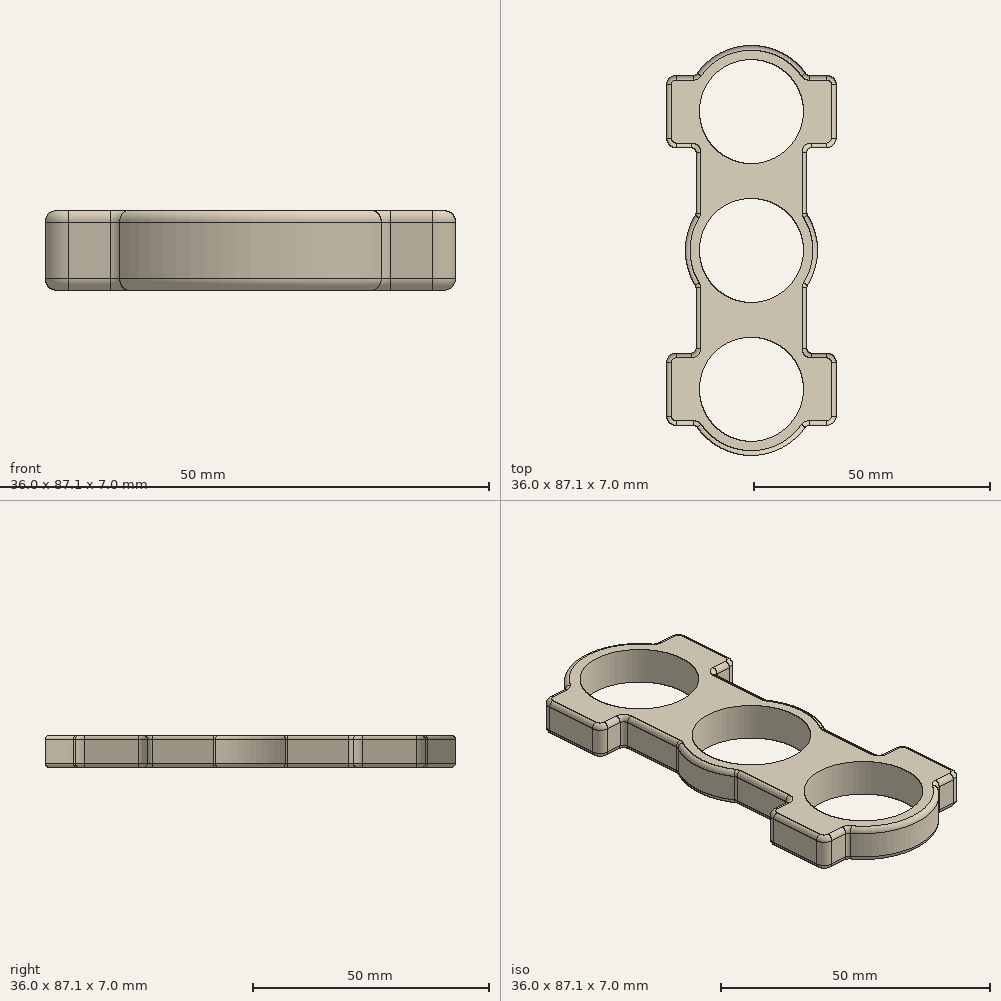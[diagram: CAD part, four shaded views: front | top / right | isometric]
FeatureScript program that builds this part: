
annotation { "Feature Type Name" : "Feature", "Feature Type Description" : "" }
export const myFeature = defineFeature(function(context is Context, id is Id, definition is map)
    precondition{}
    {
        {
            var Q0;
            Q0=qCreatedBy(makeId("Top.planeOp"),FACE);
            var sketch = newSketch(context, id + "F0", { "sketchPlane" : qUnion([Q0])});
            skCircle(sketch, "E0", {"center": v(0, 0) * mm, "radius": 11.05 * mm});
            skArc(sketch, "E1.0", {"start": v(-11.93, 7.43) * mm, "mid": v(0, -14.05) * mm, "end": v(11.93, 7.43) * mm});
            skLineSegment(sketch, "E2", {"start": v(0, 0) * mm, "end": v(0, 29.5) * mm, "construction": true});
            skCircle(sketch, "E3", {"center": v(0, 29.5) * mm, "radius": 11.05 * mm});
            skArc(sketch, "E4.0", {"start": v(11.49, 37.59) * mm, "mid": v(0, 43.55) * mm, "end": v(-11.49, 37.59) * mm});
            skLineSegment(sketch, "E5.bottom", {"start": v(18, 37.17) * mm, "end": v(12.3, 37.17) * mm});
            skLineSegment(sketch, "E5.top", {"start": v(18, 21.83) * mm, "end": v(12.77, 21.83) * mm});
            skLineSegment(sketch, "E5.left", {"start": v(18, 37.17) * mm, "end": v(18, 21.83) * mm});
            skLineSegment(sketch, "E5.right", {"start": v(-18, 37.17) * mm, "end": v(-18, 21.83) * mm});
            skLineSegment(sketch, "E6", {"start": v(-11.77, 20.83) * mm, "end": v(-11.77, 7.96) * mm});
            skLineSegment(sketch, "E7", {"start": v(11.77, 20.83) * mm, "end": v(11.77, 7.96) * mm});
            skLineSegment(sketch, "E8.trimOffspring", {"start": v(-12.77, 21.83) * mm, "end": v(-18, 21.83) * mm});
            skLineSegment(sketch, "E9.trimOffspring", {"start": v(-12.3, 37.17) * mm, "end": v(-18, 37.17) * mm});
            skPoint(sketch, "E10.visualSharp", {"position": v(-11.77, 21.83) * mm});
            skArc(sketch, "E10.filletArc", {"start": v(-11.77, 20.83) * mm, "mid": v(-12.07, 21.54) * mm, "end": v(-12.77, 21.83) * mm});
            skPoint(sketch, "E11.visualSharp", {"position": v(11.77, 21.83) * mm});
            skArc(sketch, "E11.filletArc", {"start": v(12.77, 21.83) * mm, "mid": v(12.07, 21.54) * mm, "end": v(11.77, 20.83) * mm});
            skPoint(sketch, "E12.visualSharp", {"position": v(-11.77, 37.17) * mm});
            skArc(sketch, "E12.filletArc", {"start": v(-12.3, 37.17) * mm, "mid": v(-11.84, 37.28) * mm, "end": v(-11.49, 37.59) * mm});
            skPoint(sketch, "E13.visualSharp", {"position": v(11.77, 37.17) * mm});
            skArc(sketch, "E13.filletArc", {"start": v(11.49, 37.59) * mm, "mid": v(11.84, 37.28) * mm, "end": v(12.3, 37.17) * mm});
            skPoint(sketch, "E14.visualSharp", {"position": v(-11.77, 7.67) * mm});
            skArc(sketch, "E14.filletArc", {"start": v(-11.93, 7.43) * mm, "mid": v(-11.81, 7.68) * mm, "end": v(-11.77, 7.96) * mm});
            skPoint(sketch, "E15.visualSharp", {"position": v(11.77, 7.67) * mm});
            skArc(sketch, "E15.filletArc", {"start": v(11.77, 7.96) * mm, "mid": v(11.81, 7.68) * mm, "end": v(11.93, 7.43) * mm});
            skSolve(sketch);
        }
        {
            var Q0;
            Q0=makeQuery(id+"F0.imprint","IMPRINT",FACE,{"disambiguationData":[TD([[makeQuery(id+"F0.imprint","IMPRINT",EDGE,{"derivedFrom":sQuery(id+"F0.wireOp",EDGE,"E0")}),-1.0]])]});
            extrude(context, id + "F1", {"entities" : qUnion([Q0]), "depth" : 7 * mm, "offsetDistance" : 25 * mm});
        }
        {
            var Q0;
            Q0=makeQuery(id+"F1.opExtrude","SWEPT_EDGE",EDGE,{"disambiguationData":[OSD([sQuery(id+"F0.wireOp",EDGE,"E5.right"),sQuery(id+"F0.wireOp",EDGE,"E9.trimOffspring")])]});
            var Q1;
            Q1=makeQuery(id+"F1.opExtrude","SWEPT_EDGE",EDGE,{"disambiguationData":[OSD([sQuery(id+"F0.wireOp",EDGE,"E5.right"),sQuery(id+"F0.wireOp",EDGE,"E8.trimOffspring")])]});
            var Q2;
            Q2=makeQuery(id+"F1.opExtrude","SWEPT_EDGE",EDGE,{"disambiguationData":[OSD([sQuery(id+"F0.wireOp",EDGE,"E5.bottom"),sQuery(id+"F0.wireOp",EDGE,"E5.left")])]});
            var Q3;
            Q3=makeQuery(id+"F1.opExtrude","SWEPT_EDGE",EDGE,{"disambiguationData":[OSD([sQuery(id+"F0.wireOp",EDGE,"E5.top"),sQuery(id+"F0.wireOp",EDGE,"E5.left")])]});
            fillet(context, id + "F2", {"entities" : qUnion([Q0, Q1, Q2, Q3]), "radius" : 2 * mm, "tangentPropagation" : true, "allowEdgeOverflow" : false});
        }
        {
            var Q0;
            Q0=qCreatedBy(makeId("Right.planeOp"),FACE);
            var sketch = newSketch(context, id + "F3", { "sketchPlane" : qUnion([Q0])});
            skLineSegment(sketch, "E16", {"start": v(0, -10.12) * mm, "end": v(0, 12.98) * mm, "construction": true});
            skSolve(sketch);
        }
        {
            var Q0;
            Q0=makeQuery(id+"F1.opExtrude","SWEPT_BODY",BODY,{"disambiguationData":[OSD([sQuery(id+"F0.wireOp",EDGE,"E0"),sQuery(id+"F0.wireOp",EDGE,"E1.0"),sQuery(id+"F0.wireOp",EDGE,"E3"),sQuery(id+"F0.wireOp",EDGE,"E4.0"),sQuery(id+"F0.wireOp",EDGE,"E5.bottom"),sQuery(id+"F0.wireOp",EDGE,"E5.top"),sQuery(id+"F0.wireOp",EDGE,"E5.left"),sQuery(id+"F0.wireOp",EDGE,"E5.right"),sQuery(id+"F0.wireOp",EDGE,"E6"),sQuery(id+"F0.wireOp",EDGE,"E7"),sQuery(id+"F0.wireOp",EDGE,"E8.trimOffspring"),sQuery(id+"F0.wireOp",EDGE,"E9.trimOffspring"),sQuery(id+"F0.wireOp",EDGE,"E10.filletArc"),sQuery(id+"F0.wireOp",EDGE,"E11.filletArc"),sQuery(id+"F0.wireOp",EDGE,"E12.filletArc"),sQuery(id+"F0.wireOp",EDGE,"E13.filletArc"),sQuery(id+"F0.wireOp",EDGE,"E14.filletArc"),sQuery(id+"F0.wireOp",EDGE,"E15.filletArc")])]});
            var Q1;
            Q1=sQuery(id+"F3.wireOp",EDGE,"E16");
            circularPattern(context, id + "F4", {"operationType" : NewBodyOperationType.ADD, "entities" : qUnion([Q0]), "axis" : qUnion([Q1]), "angle" : 360 * degree, "instanceCount" : 2, "equalSpace" : true});
        }
        {
            var Q0;
            Q0=makeQuery(id+"F4.opPattern","COPY",EDGE,{"derivedFrom":makeQuery(id+"F1.opExtrude","CAP_EDGE",EDGE,{"disambiguationData":[OSD([sQuery(id+"F0.wireOp",EDGE,"E7")])],"isStart":false}),"instanceName":"1"});
            var Q1;
            Q1=makeQuery(id+"F4.opPattern","COPY",EDGE,{"derivedFrom":makeQuery(id+"F1.opExtrude","CAP_EDGE",EDGE,{"disambiguationData":[OSD([sQuery(id+"F0.wireOp",EDGE,"E7")])],"isStart":true}),"instanceName":"1"});
            fillet(context, id + "F5", {"entities" : qUnion([Q0, Q1]), "radius" : 1 * mm, "tangentPropagation" : true, "allowEdgeOverflow" : false});
        }
    });
